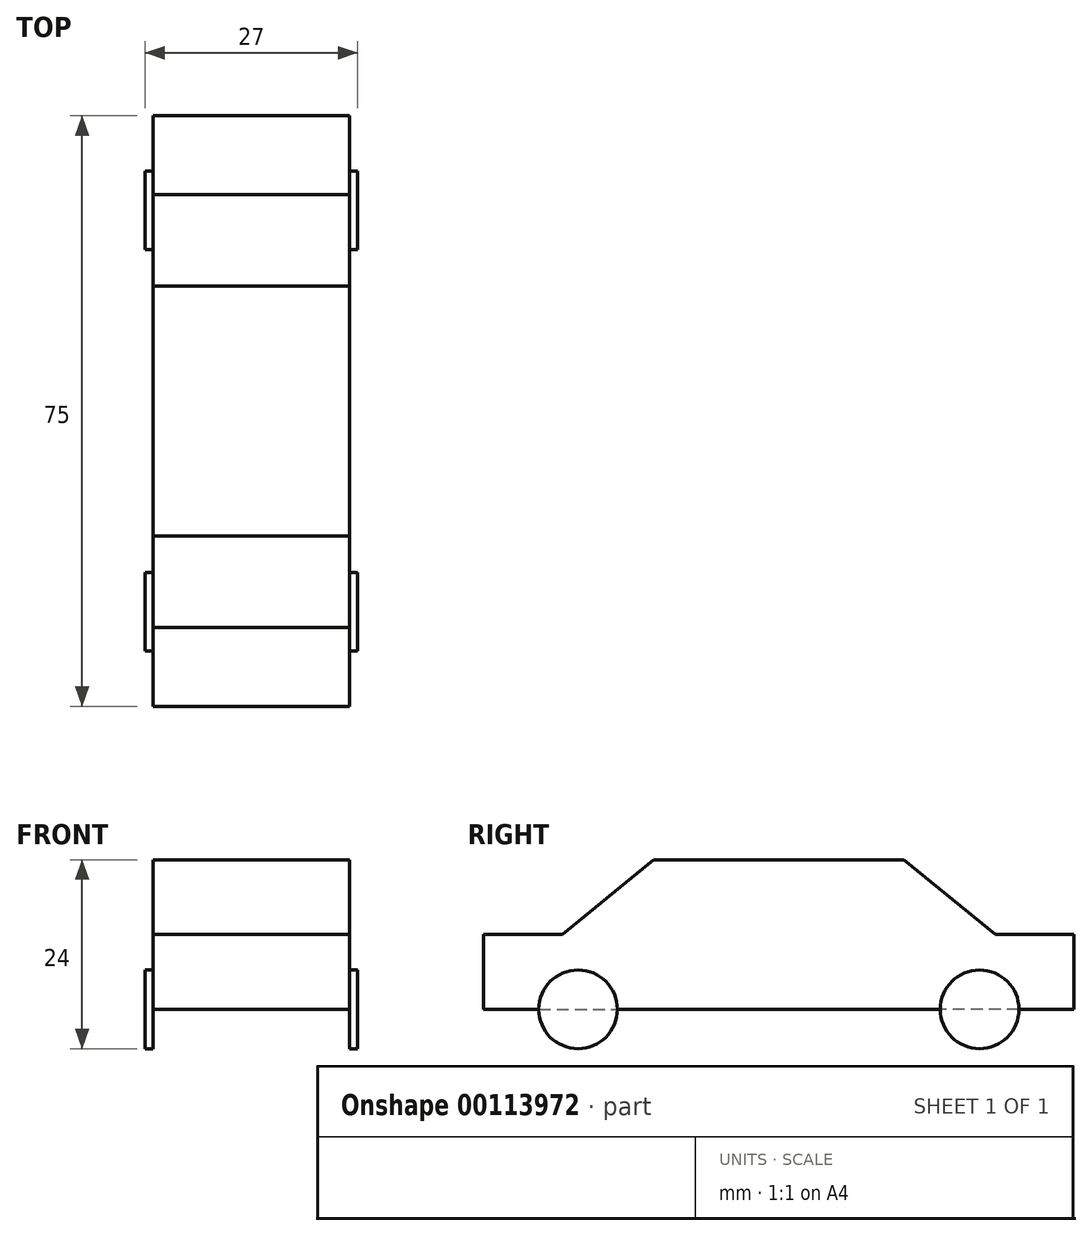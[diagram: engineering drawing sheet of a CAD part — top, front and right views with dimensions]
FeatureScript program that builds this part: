
annotation { "Feature Type Name" : "Feature", "Feature Type Description" : "" }
export const myFeature = defineFeature(function(context is Context, id is Id, definition is map)
    precondition{}
    {
        {
            var Q0;
            Q0=qCreatedBy(makeId("Top.planeOp"),FACE);
            var sketch = newSketch(context, id + "F0", { "sketchPlane" : qUnion([Q0])});
            skLineSegment(sketch, "E0.bottom", {"start": v(-12.5, 37.5) * mm, "end": v(12.5, 37.5) * mm});
            skLineSegment(sketch, "E0.top", {"start": v(-12.5, 0) * mm, "end": v(12.5, 0) * mm});
            skLineSegment(sketch, "E0.left", {"start": v(-12.5, 37.5) * mm, "end": v(-12.5, 0) * mm});
            skLineSegment(sketch, "E0.right", {"start": v(12.5, 37.5) * mm, "end": v(12.5, 0) * mm});
            skSolve(sketch);
        }
        {
            var Q0;
            Q0 = qSketchRegion(id + "F0", true);
            extrude(context, id + "F1", {"entities" : qUnion([Q0]), "depth" : 19 * mm});
        }
        {
            var Q0;
            Q0=makeQuery(id+"F1.opExtrude","SWEPT_FACE",FACE,{"disambiguationData":[OSD([sQuery(id+"F0.wireOp",EDGE,"E0.right")])]});
            var sketch = newSketch(context, id + "F2", { "sketchPlane" : qUnion([Q0])});
            skCircle(sketch, "E1", {"center": v(25.5, 0) * mm, "radius": 5 * mm});
            skSolve(sketch);
        }
        {
            var Q0;
            Q0 = qSketchRegion(id + "F2", true);
            extrude(context, id + "F3", {"entities" : qUnion([Q0]), "depth" : 1 * mm});
        }
        {
            var Q0;
            Q0=makeQuery(id+"F1.opExtrude","SWEPT_FACE",FACE,{"disambiguationData":[OSD([sQuery(id+"F0.wireOp",EDGE,"E0.right")])]});
            var sketch = newSketch(context, id + "F4", { "sketchPlane" : qUnion([Q0])});
            skLineSegment(sketch, "E2", {"start": v(37.5, 9.5) * mm, "end": v(27.5, 9.5) * mm});
            skLineSegment(sketch, "E3", {"start": v(27.5, 9.5) * mm, "end": v(15.9, 19) * mm});
            skLineSegment(sketch, "E4", {"start": v(15.9, 19) * mm, "end": v(37.5, 19) * mm});
            skLineSegment(sketch, "E5", {"start": v(37.5, 19) * mm, "end": v(37.5, 9.5) * mm});
            skSolve(sketch);
        }
        {
            var Q0;
            Q0 = qSketchRegion(id + "F4", true);
            extrude(context, id + "F5", {"entities" : qUnion([Q0]), "operationType" : NewBodyOperationType.REMOVE, "endBound" : BoundingType.THROUGH_ALL, "oppositeDirection" : true, "depth" : 25 * mm});
        }
        {
            var Q0;
            Q0=makeQuery(id+"F1.opExtrude","SWEPT_BODY",BODY,{"disambiguationData":[OSD([sQuery(id+"F0.wireOp",EDGE,"E0.bottom"),sQuery(id+"F0.wireOp",EDGE,"E0.top"),sQuery(id+"F0.wireOp",EDGE,"E0.left"),sQuery(id+"F0.wireOp",EDGE,"E0.right")])]});
            var Q1;
            Q1=makeQuery(id+"F3.opExtrude","SWEPT_BODY",BODY,{"disambiguationData":[OSD([sQuery(id+"F2.wireOp",EDGE,"E1")])]});
            var Q2;
            Q2=qCreatedBy(makeId("Right.planeOp"),FACE);
            mirror(context, id + "F6", {"operationType" : NewBodyOperationType.ADD, "entities" : qUnion([Q0, Q1]), "mirrorPlane" : qUnion([Q2])});
        }
        {
            var Q0;
            Q0=makeQuery(id+"F6.opPattern","COPY",BODY,{"derivedFrom":makeQuery(id+"F1.opExtrude","SWEPT_BODY",BODY,{"disambiguationData":[OSD([sQuery(id+"F0.wireOp",EDGE,"E0.bottom"),sQuery(id+"F0.wireOp",EDGE,"E0.top"),sQuery(id+"F0.wireOp",EDGE,"E0.left"),sQuery(id+"F0.wireOp",EDGE,"E0.right")])]}),"instanceName":"1"});
            var Q1;
            Q1=makeQuery(id+"F3.opExtrude","SWEPT_BODY",BODY,{"disambiguationData":[OSD([sQuery(id+"F2.wireOp",EDGE,"E1")])]});
            var Q2;
            Q2=makeQuery(id+"F6.opPattern","COPY",BODY,{"derivedFrom":makeQuery(id+"F3.opExtrude","SWEPT_BODY",BODY,{"disambiguationData":[OSD([sQuery(id+"F2.wireOp",EDGE,"E1")])]}),"instanceName":"1"});
            var Q3;
            Q3=makeQuery(id+"F1.opExtrude","SWEPT_BODY",BODY,{"disambiguationData":[OSD([sQuery(id+"F0.wireOp",EDGE,"E0.bottom"),sQuery(id+"F0.wireOp",EDGE,"E0.top"),sQuery(id+"F0.wireOp",EDGE,"E0.left"),sQuery(id+"F0.wireOp",EDGE,"E0.right")])]});
            var Q4;
            Q4=qCreatedBy(makeId("Front.planeOp"),FACE);
            mirror(context, id + "F7", {"operationType" : NewBodyOperationType.ADD, "entities" : qUnion([Q0, Q1, Q2, Q3]), "mirrorPlane" : qUnion([Q4])});
        }
    });
